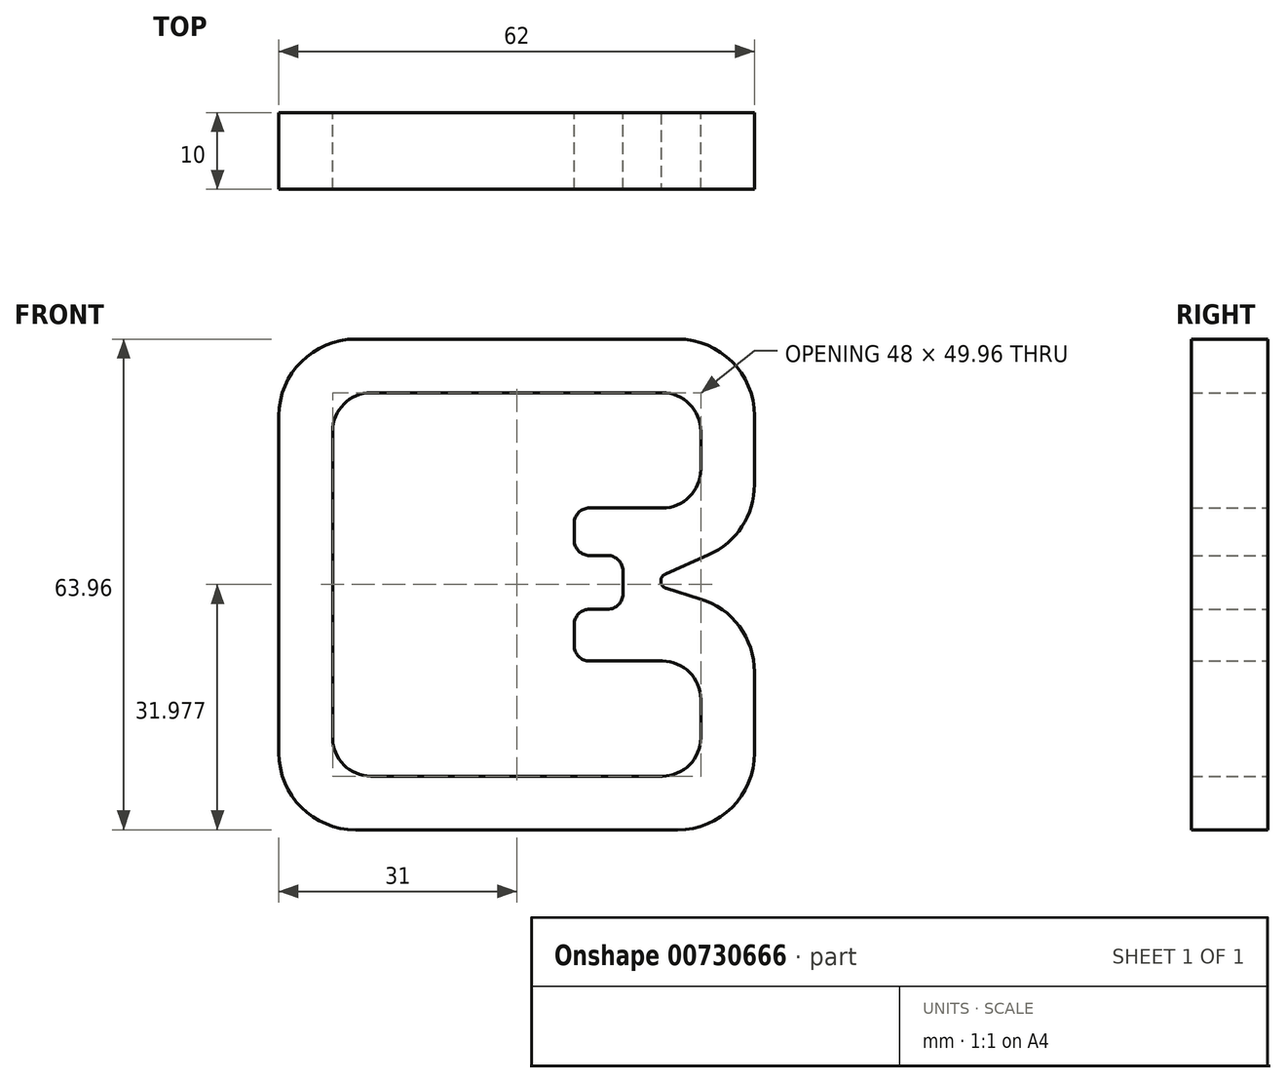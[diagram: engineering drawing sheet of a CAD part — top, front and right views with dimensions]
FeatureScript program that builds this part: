
annotation { "Feature Type Name" : "Feature", "Feature Type Description" : "" }
export const myFeature = defineFeature(function(context is Context, id is Id, definition is map)
    precondition{}
    {
        {
            var Q0;
            Q0=qCreatedBy(makeId("Front.planeOp"),FACE);
            var sketch = newSketch(context, id + "F0", { "sketchPlane" : qUnion([Q0])});
            skLineSegment(sketch, "E0", {"start": v(27.5, 27.14) * mm, "end": v(-20.5, 27.14) * mm});
            skLineSegment(sketch, "E1", {"start": v(-20.5, 27.14) * mm, "end": v(-20.5, -22.82) * mm});
            skLineSegment(sketch, "E2", {"start": v(-20.5, -22.82) * mm, "end": v(27.5, -22.82) * mm});
            skLineSegment(sketch, "E3", {"start": v(27.5, -22.82) * mm, "end": v(27.5, -7.82) * mm});
            skLineSegment(sketch, "E4", {"start": v(27.5, -7.82) * mm, "end": v(11, -7.82) * mm});
            skLineSegment(sketch, "E5", {"start": v(11, -7.82) * mm, "end": v(11, -1.07) * mm});
            skLineSegment(sketch, "E6", {"start": v(11, -1.07) * mm, "end": v(17.35, -1.07) * mm});
            skLineSegment(sketch, "E7", {"start": v(17.35, -1.07) * mm, "end": v(17.35, 5.93) * mm});
            skLineSegment(sketch, "E8", {"start": v(17.35, 5.93) * mm, "end": v(11, 5.93) * mm});
            skLineSegment(sketch, "E9", {"start": v(11, 5.93) * mm, "end": v(11, 12.14) * mm});
            skLineSegment(sketch, "E10", {"start": v(11, 12.14) * mm, "end": v(27.5, 12.14) * mm});
            skLineSegment(sketch, "E11", {"start": v(27.5, 12.14) * mm, "end": v(27.5, 27.14) * mm});
            skLineSegment(sketch, "E12", {"start": v(-27.5, -29.82) * mm, "end": v(-27.5, 34.14) * mm});
            skLineSegment(sketch, "E13", {"start": v(-27.5, 34.14) * mm, "end": v(34.5, 34.14) * mm});
            skLineSegment(sketch, "E14", {"start": v(34.5, 34.14) * mm, "end": v(34.5, 8.65) * mm});
            skLineSegment(sketch, "E15", {"start": v(34.5, 8.65) * mm, "end": v(20.44, 2.43) * mm});
            skLineSegment(sketch, "E16", {"start": v(20.44, 2.43) * mm, "end": v(34.5, -1.87) * mm});
            skLineSegment(sketch, "E17", {"start": v(34.5, -1.87) * mm, "end": v(34.5, -29.82) * mm});
            skLineSegment(sketch, "E18", {"start": v(34.5, -29.82) * mm, "end": v(-27.5, -29.82) * mm});
            skPoint(sketch, "E19", {"position": v(17.35, 2.43) * mm});
            skSolve(sketch);
        }
        {
            var Q0;
            Q0=qSketchRegion(id+"F0",true);
            extrude(context, id + "F1", {"entities" : qUnion([Q0]), "depth" : 10 * mm, "offsetDistance" : 25 * mm});
        }
        {
            var Q0;
            Q0=makeQuery(id+"F1.opExtrude","SWEPT_EDGE",EDGE,{"disambiguationData":[OSD([sQuery(id+"F0.wireOp",EDGE,"E0"),sQuery(id+"F0.wireOp",EDGE,"E1")])]});
            var Q1;
            Q1=makeQuery(id+"F1.opExtrude","SWEPT_EDGE",EDGE,{"disambiguationData":[OSD([sQuery(id+"F0.wireOp",EDGE,"E0"),sQuery(id+"F0.wireOp",EDGE,"E11")])]});
            var Q2;
            Q2=makeQuery(id+"F1.opExtrude","SWEPT_EDGE",EDGE,{"disambiguationData":[OSD([sQuery(id+"F0.wireOp",EDGE,"E10"),sQuery(id+"F0.wireOp",EDGE,"E11")])]});
            var Q3;
            Q3=makeQuery(id+"F1.opExtrude","SWEPT_EDGE",EDGE,{"disambiguationData":[OSD([sQuery(id+"F0.wireOp",EDGE,"E1"),sQuery(id+"F0.wireOp",EDGE,"E2")])]});
            var Q4;
            Q4=makeQuery(id+"F1.opExtrude","SWEPT_EDGE",EDGE,{"disambiguationData":[OSD([sQuery(id+"F0.wireOp",EDGE,"E2"),sQuery(id+"F0.wireOp",EDGE,"E3")])]});
            var Q5;
            Q5=makeQuery(id+"F1.opExtrude","SWEPT_EDGE",EDGE,{"disambiguationData":[OSD([sQuery(id+"F0.wireOp",EDGE,"E3"),sQuery(id+"F0.wireOp",EDGE,"E4")])]});
            fillet(context, id + "F2", {"entities" : qUnion([Q0, Q1, Q2, Q3, Q4, Q5]), "radius" : 5 * mm, "tangentPropagation" : true, "allowEdgeOverflow" : false});
        }
        {
            var Q0;
            Q0=makeQuery(id+"F1.opExtrude","SWEPT_EDGE",EDGE,{"disambiguationData":[OSD([sQuery(id+"F0.wireOp",EDGE,"E9"),sQuery(id+"F0.wireOp",EDGE,"E10")])]});
            var Q1;
            Q1=makeQuery(id+"F1.opExtrude","SWEPT_EDGE",EDGE,{"disambiguationData":[OSD([sQuery(id+"F0.wireOp",EDGE,"E8"),sQuery(id+"F0.wireOp",EDGE,"E9")])]});
            var Q2;
            Q2=makeQuery(id+"F1.opExtrude","SWEPT_EDGE",EDGE,{"disambiguationData":[OSD([sQuery(id+"F0.wireOp",EDGE,"E7"),sQuery(id+"F0.wireOp",EDGE,"E8")])]});
            var Q3;
            Q3=makeQuery(id+"F1.opExtrude","SWEPT_EDGE",EDGE,{"disambiguationData":[OSD([sQuery(id+"F0.wireOp",EDGE,"E6"),sQuery(id+"F0.wireOp",EDGE,"E7")])]});
            var Q4;
            Q4=makeQuery(id+"F1.opExtrude","SWEPT_EDGE",EDGE,{"disambiguationData":[OSD([sQuery(id+"F0.wireOp",EDGE,"E5"),sQuery(id+"F0.wireOp",EDGE,"E6")])]});
            var Q5;
            Q5=makeQuery(id+"F1.opExtrude","SWEPT_EDGE",EDGE,{"disambiguationData":[OSD([sQuery(id+"F0.wireOp",EDGE,"E4"),sQuery(id+"F0.wireOp",EDGE,"E5")])]});
            fillet(context, id + "F3", {"entities" : qUnion([Q0, Q1, Q2, Q3, Q4, Q5]), "radius" : 2 * mm, "tangentPropagation" : true, "allowEdgeOverflow" : false});
        }
        {
            var Q0;
            Q0=makeQuery(id+"F1.opExtrude","SWEPT_EDGE",EDGE,{"disambiguationData":[OSD([sQuery(id+"F0.wireOp",EDGE,"E13"),sQuery(id+"F0.wireOp",EDGE,"E14")])]});
            var Q1;
            Q1=makeQuery(id+"F1.opExtrude","SWEPT_EDGE",EDGE,{"disambiguationData":[OSD([sQuery(id+"F0.wireOp",EDGE,"E14"),sQuery(id+"F0.wireOp",EDGE,"E15")])]});
            var Q2;
            Q2=makeQuery(id+"F1.opExtrude","SWEPT_EDGE",EDGE,{"disambiguationData":[OSD([sQuery(id+"F0.wireOp",EDGE,"E16"),sQuery(id+"F0.wireOp",EDGE,"E17")])]});
            var Q3;
            Q3=makeQuery(id+"F1.opExtrude","SWEPT_EDGE",EDGE,{"disambiguationData":[OSD([sQuery(id+"F0.wireOp",EDGE,"E17"),sQuery(id+"F0.wireOp",EDGE,"E18")])]});
            fillet(context, id + "F4", {"entities" : qUnion([Q0, Q1, Q2, Q3]), "radius" : 10 * mm, "tangentPropagation" : true, "allowEdgeOverflow" : false});
        }
        {
            var Q0;
            Q0=makeQuery(id+"F1.opExtrude","SWEPT_EDGE",EDGE,{"disambiguationData":[OSD([sQuery(id+"F0.wireOp",EDGE,"E15"),sQuery(id+"F0.wireOp",EDGE,"E16")])]});
            fillet(context, id + "F5", {"entities" : qUnion([Q0]), "radius" : 1 * mm, "tangentPropagation" : true, "allowEdgeOverflow" : false});
        }
        {
            var Q0;
            Q0=makeQuery(id+"F1.opExtrude","SWEPT_EDGE",EDGE,{"disambiguationData":[OSD([sQuery(id+"F0.wireOp",EDGE,"E12"),sQuery(id+"F0.wireOp",EDGE,"E13")])]});
            var Q1;
            Q1=makeQuery(id+"F1.opExtrude","SWEPT_EDGE",EDGE,{"disambiguationData":[OSD([sQuery(id+"F0.wireOp",EDGE,"E12"),sQuery(id+"F0.wireOp",EDGE,"E18")])]});
            fillet(context, id + "F6", {"entities" : qUnion([Q0, Q1]), "radius" : 10 * mm, "tangentPropagation" : true, "allowEdgeOverflow" : false});
        }
    });
